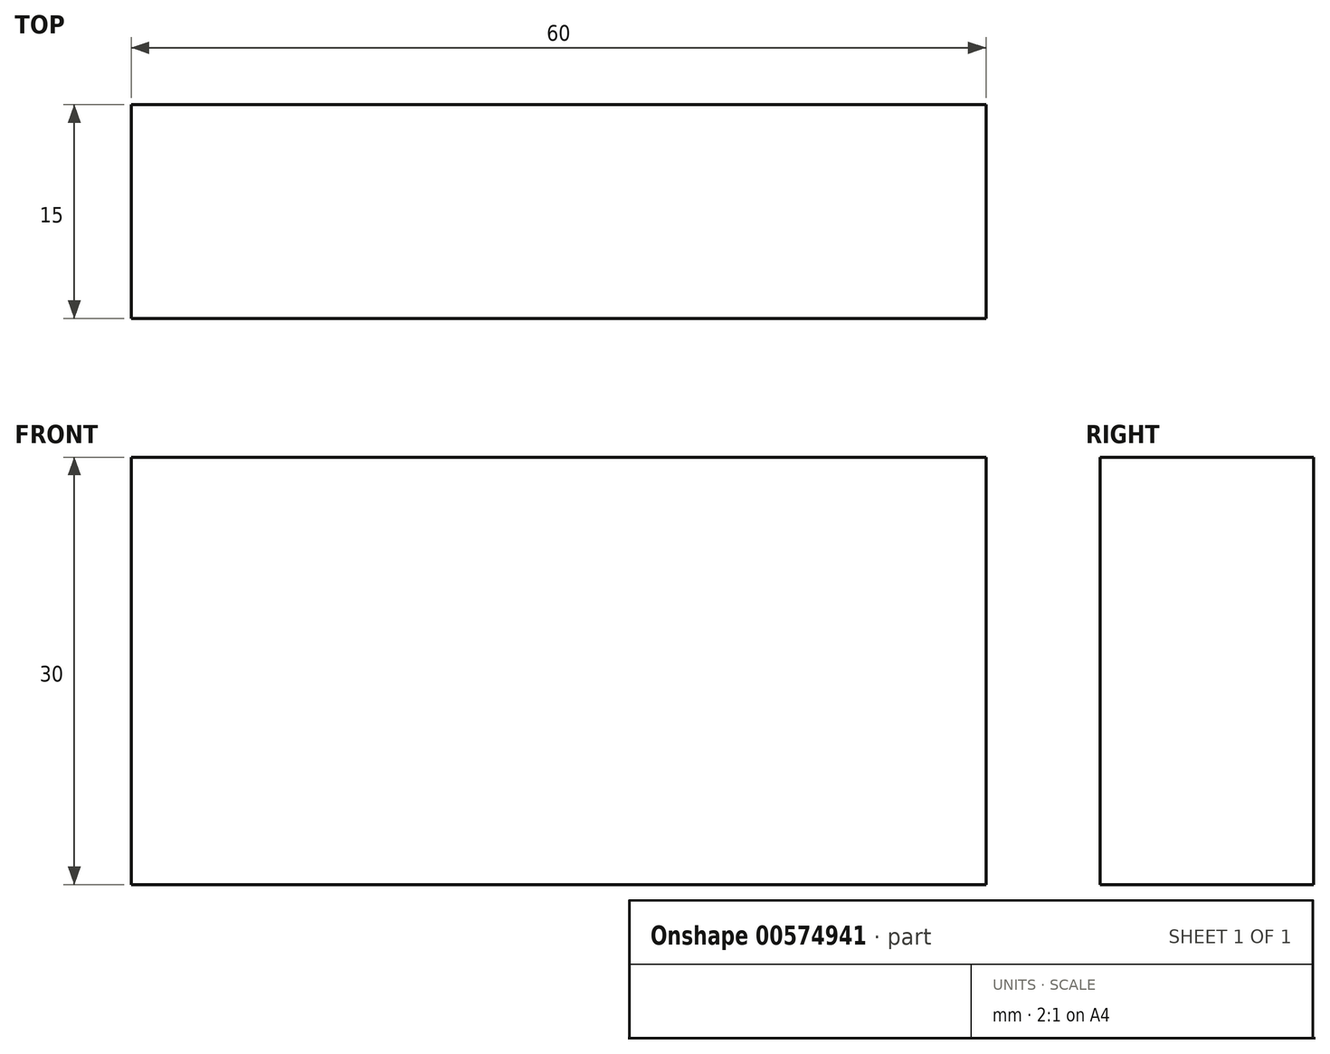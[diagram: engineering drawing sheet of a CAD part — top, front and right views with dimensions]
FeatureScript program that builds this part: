
annotation { "Feature Type Name" : "Feature", "Feature Type Description" : "" }
export const myFeature = defineFeature(function(context is Context, id is Id, definition is map)
    precondition{}
    {
        {
            var Q0;
            Q0=qCreatedBy(makeId("Front.planeOp"),FACE);
            var sketch = newSketch(context, id + "F0", { "sketchPlane" : qUnion([Q0])});
            skLineSegment(sketch, "E0.bottom", {"start": v(-30, 15) * mm, "end": v(30, 15) * mm});
            skLineSegment(sketch, "E0.top", {"start": v(-30, -15) * mm, "end": v(30, -15) * mm});
            skLineSegment(sketch, "E0.left", {"start": v(-30, 15) * mm, "end": v(-30, -15) * mm});
            skLineSegment(sketch, "E0.right", {"start": v(30, 15) * mm, "end": v(30, -15) * mm});
            skPoint(sketch, "E0.middle", {"position": v(0, 0) * mm});
            skSolve(sketch);
        }
        {
            var Q0;
            Q0=makeQuery(id+"F0.imprint","IMPRINT",FACE,{"disambiguationData":[TD([[makeQuery(id+"F0.imprint","IMPRINT",EDGE,{"derivedFrom":sQuery(id+"F0.wireOp",EDGE,"E0.bottom")}),-1.0]])]});
            extrude(context, id + "F1", {"entities" : qUnion([Q0]), "depth" : 15 * mm, "offsetDistance" : 25 * mm});
        }
    });
